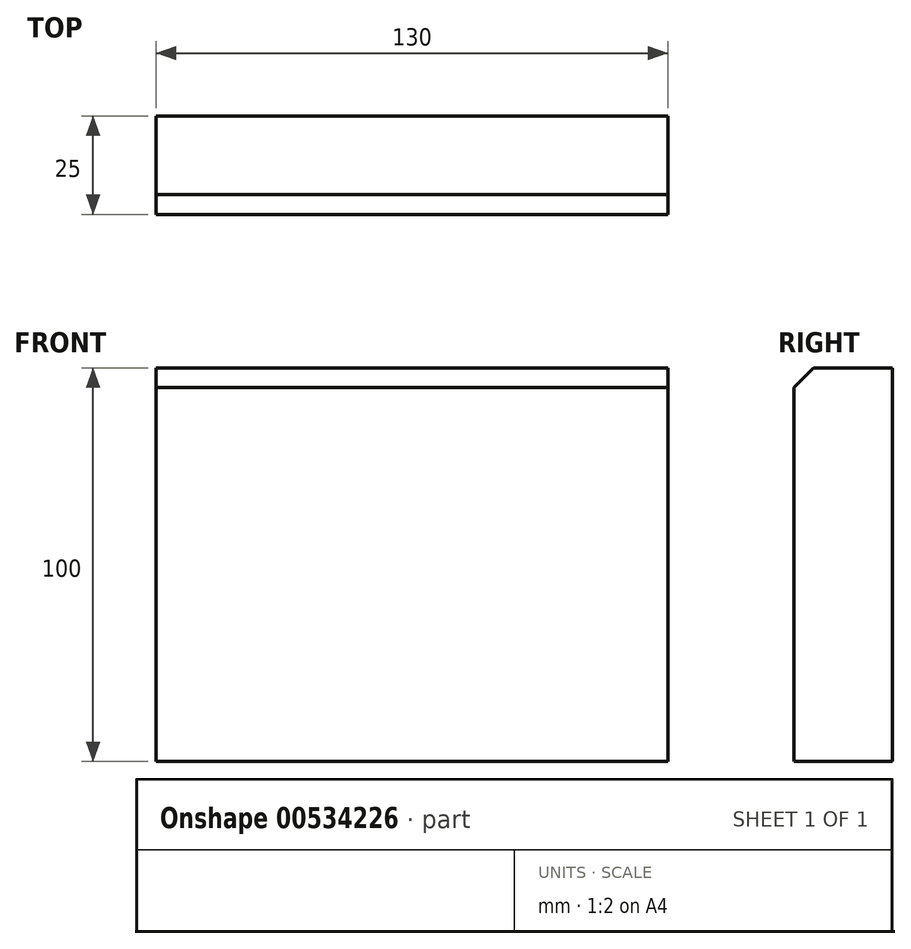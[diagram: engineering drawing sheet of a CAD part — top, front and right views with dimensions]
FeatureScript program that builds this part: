
annotation { "Feature Type Name" : "Feature", "Feature Type Description" : "" }
export const myFeature = defineFeature(function(context is Context, id is Id, definition is map)
    precondition{}
    {
        {
            var Q0;
            Q0=qCreatedBy(makeId("Front.planeOp"),FACE);
            var sketch = newSketch(context, id + "F0", { "sketchPlane" : qUnion([Q0])});
            skLineSegment(sketch, "E0.bottom", {"start": v(-65, 50) * mm, "end": v(65, 50) * mm});
            skLineSegment(sketch, "E0.top", {"start": v(-65, -50) * mm, "end": v(65, -50) * mm});
            skLineSegment(sketch, "E0.left", {"start": v(-65, 50) * mm, "end": v(-65, -50) * mm});
            skLineSegment(sketch, "E0.right", {"start": v(65, 50) * mm, "end": v(65, -50) * mm});
            skPoint(sketch, "E0.middle", {"position": v(0, 0) * mm});
            skSolve(sketch);
        }
        {
            var Q0;
            Q0 = qSketchRegion(id + "F0", true);
            extrude(context, id + "F1", {"entities" : qUnion([Q0]), "depth" : 25 * mm, "offsetDistance" : 25 * mm});
        }
        {
            var Q0;
            Q0=makeQuery(id+"F1.opExtrude","CAP_EDGE",EDGE,{"disambiguationData":[OSD([sQuery(id+"F0.wireOp",EDGE,"E0.bottom")])],"isStart":false});
            chamfer(context, id + "F2", {"entities" : qUnion([Q0]), "width" : 5 * mm, "tangentPropagation" : true});
        }
    });
